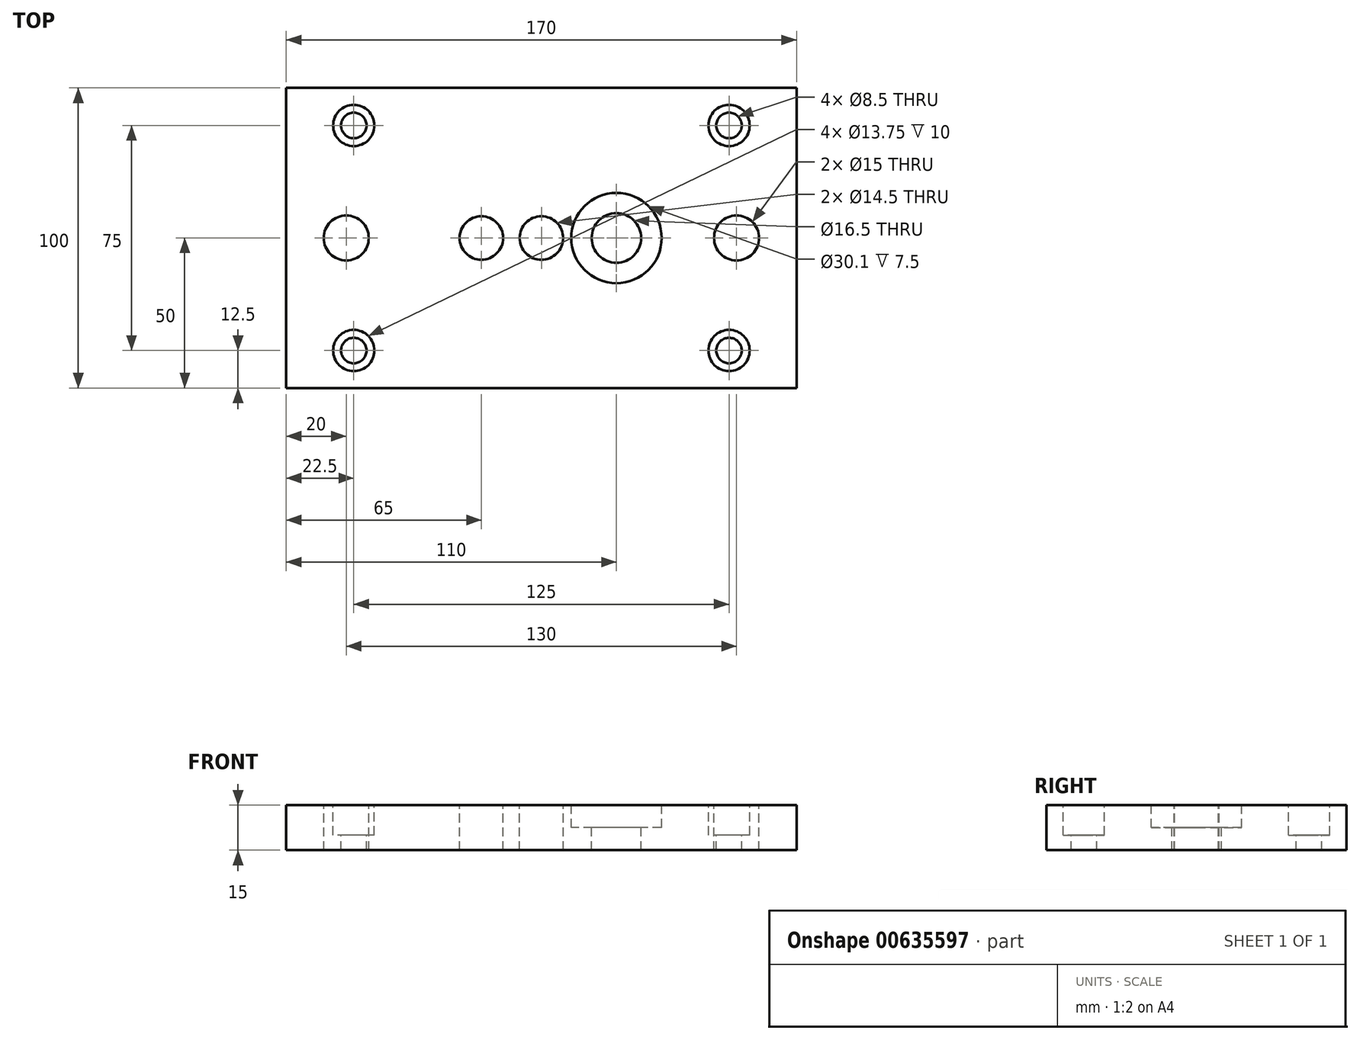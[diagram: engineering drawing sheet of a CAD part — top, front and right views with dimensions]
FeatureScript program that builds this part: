
annotation { "Feature Type Name" : "Feature", "Feature Type Description" : "" }
export const myFeature = defineFeature(function(context is Context, id is Id, definition is map)
    precondition{}
    {
        {
            var Q0;
            Q0=qCreatedBy(makeId("Top.planeOp"),FACE);
            var sketch = newSketch(context, id + "F0", { "sketchPlane" : qUnion([Q0])});
            skLineSegment(sketch, "E0.bottom", {"start": v(0, 0) * mm, "end": v(170, 0) * mm});
            skLineSegment(sketch, "E0.top", {"start": v(0, 100) * mm, "end": v(170, 100) * mm});
            skLineSegment(sketch, "E0.left", {"start": v(0, 0) * mm, "end": v(0, 100) * mm});
            skLineSegment(sketch, "E0.right", {"start": v(170, 0) * mm, "end": v(170, 100) * mm});
            skSolve(sketch);
        }
        {
            var Q0;
            Q0=makeQuery(id+"F0.imprint","IMPRINT",FACE,{"disambiguationData":[TD([[makeQuery(id+"F0.imprint","IMPRINT",EDGE,{"derivedFrom":sQuery(id+"F0.wireOp",EDGE,"E0.bottom")}),1.0]])]});
            extrude(context, id + "F1", {"entities" : qUnion([Q0]), "oppositeDirection" : true, "depth" : 15 * mm, "offsetDistance" : 25 * mm});
        }
        {
            var Q0;
            Q0=makeQuery(id+"F1.opExtrude","CAP_FACE",FACE,{"disambiguationData":[OSD([sQuery(id+"F0.wireOp",EDGE,"E0.bottom"),sQuery(id+"F0.wireOp",EDGE,"E0.top"),sQuery(id+"F0.wireOp",EDGE,"E0.left"),sQuery(id+"F0.wireOp",EDGE,"E0.right")])],"isStart":true});
            var sketch = newSketch(context, id + "F2", { "sketchPlane" : qUnion([Q0])});
            skPoint(sketch, "E1", {"position": v(22.5, 12.5) * mm});
            skPoint(sketch, "E2", {"position": v(22.5, 87.5) * mm});
            skPoint(sketch, "E3", {"position": v(147.5, 87.5) * mm});
            skPoint(sketch, "E4", {"position": v(147.5, 12.5) * mm});
            skSolve(sketch);
        }
        {
            var Q0;
            Q0=sQuery(id+"F2.wireOp",VERTEX,"E2");
            var Q1;
            Q1=sQuery(id+"F2.wireOp",VERTEX,"E1");
            var Q2;
            Q2=sQuery(id+"F2.wireOp",VERTEX,"E3");
            var Q3;
            Q3=sQuery(id+"F2.wireOp",VERTEX,"E4");
            var Q4;
            Q4=makeQuery(id+"F1.opExtrude","SWEPT_BODY",BODY,{"disambiguationData":[OSD([sQuery(id+"F0.wireOp",EDGE,"E0.bottom"),sQuery(id+"F0.wireOp",EDGE,"E0.top"),sQuery(id+"F0.wireOp",EDGE,"E0.left"),sQuery(id+"F0.wireOp",EDGE,"E0.right")])]});
            hole(context, id + "F3", {"style" : HoleStyle.C_BORE, "endStyle" : HoleEndStyle.THROUGH, "holeDiameter" : 8.5 * mm, "cBoreDiameter" : 13.75 * mm, "cBoreDepth" : 10 * mm, "majorDiameter" : 5 * mm, "isTappedThrough" : true, "tappedDepth" : 12.7 * mm, "tapClearance" : 3, "startFromSketch" : true, "locations" : qUnion([Q0, Q1, Q2, Q3]), "scope" : qUnion([Q4])});
        }
        {
            var Q0;
            Q0=makeQuery(id+"F1.opExtrude","CAP_FACE",FACE,{"disambiguationData":[OSD([sQuery(id+"F0.wireOp",EDGE,"E0.bottom"),sQuery(id+"F0.wireOp",EDGE,"E0.top"),sQuery(id+"F0.wireOp",EDGE,"E0.left"),sQuery(id+"F0.wireOp",EDGE,"E0.right")])],"isStart":true});
            var sketch = newSketch(context, id + "F4", { "sketchPlane" : qUnion([Q0])});
            skPoint(sketch, "E5", {"position": v(20, 50) * mm});
            skPoint(sketch, "E6", {"position": v(150, 50) * mm});
            skSolve(sketch);
        }
        {
            var Q0;
            Q0=sQuery(id+"F4.wireOp",VERTEX,"E5");
            var Q1;
            Q1=sQuery(id+"F4.wireOp",VERTEX,"E6");
            var Q2;
            Q2=makeQuery(id+"F1.opExtrude","SWEPT_BODY",BODY,{"disambiguationData":[OSD([sQuery(id+"F0.wireOp",EDGE,"E0.bottom"),sQuery(id+"F0.wireOp",EDGE,"E0.top"),sQuery(id+"F0.wireOp",EDGE,"E0.left"),sQuery(id+"F0.wireOp",EDGE,"E0.right")])]});
            hole(context, id + "F5", {"style" : HoleStyle.SIMPLE, "endStyle" : HoleEndStyle.THROUGH, "holeDiameter" : 15 * mm, "majorDiameter" : 5 * mm, "isTappedThrough" : true, "tappedDepth" : 12.7 * mm, "tapClearance" : 3, "startFromSketch" : true, "locations" : qUnion([Q0, Q1]), "scope" : qUnion([Q2])});
        }
        {
            var Q0;
            Q0=makeQuery(id+"F1.opExtrude","CAP_FACE",FACE,{"disambiguationData":[OSD([sQuery(id+"F0.wireOp",EDGE,"E0.bottom"),sQuery(id+"F0.wireOp",EDGE,"E0.top"),sQuery(id+"F0.wireOp",EDGE,"E0.left"),sQuery(id+"F0.wireOp",EDGE,"E0.right")])],"isStart":true});
            var sketch = newSketch(context, id + "F6", { "sketchPlane" : qUnion([Q0])});
            skPoint(sketch, "E7", {"position": v(65, 50) * mm});
            skPoint(sketch, "E8", {"position": v(85, 50) * mm});
            skSolve(sketch);
        }
        {
            var Q0;
            Q0=sQuery(id+"F6.wireOp",VERTEX,"E7");
            var Q1;
            Q1=sQuery(id+"F6.wireOp",VERTEX,"E8");
            var Q2;
            Q2=makeQuery(id+"F1.opExtrude","SWEPT_BODY",BODY,{"disambiguationData":[OSD([sQuery(id+"F0.wireOp",EDGE,"E0.bottom"),sQuery(id+"F0.wireOp",EDGE,"E0.top"),sQuery(id+"F0.wireOp",EDGE,"E0.left"),sQuery(id+"F0.wireOp",EDGE,"E0.right")])]});
            hole(context, id + "F7", {"style" : HoleStyle.SIMPLE, "endStyle" : HoleEndStyle.THROUGH, "holeDiameter" : 14.5 * mm, "majorDiameter" : 5 * mm, "isTappedThrough" : true, "tappedDepth" : 12.7 * mm, "tapClearance" : 3, "startFromSketch" : true, "locations" : qUnion([Q0, Q1]), "scope" : qUnion([Q2])});
        }
        {
            var Q0;
            Q0=makeQuery(id+"F1.opExtrude","CAP_FACE",FACE,{"disambiguationData":[OSD([sQuery(id+"F0.wireOp",EDGE,"E0.bottom"),sQuery(id+"F0.wireOp",EDGE,"E0.top"),sQuery(id+"F0.wireOp",EDGE,"E0.left"),sQuery(id+"F0.wireOp",EDGE,"E0.right")])],"isStart":true});
            var sketch = newSketch(context, id + "F8", { "sketchPlane" : qUnion([Q0])});
            skPoint(sketch, "E9", {"position": v(110, 50) * mm});
            skSolve(sketch);
        }
        {
            var Q0;
            Q0=sQuery(id+"F8.wireOp",VERTEX,"E9");
            var Q1;
            Q1=makeQuery(id+"F1.opExtrude","SWEPT_BODY",BODY,{"disambiguationData":[OSD([sQuery(id+"F0.wireOp",EDGE,"E0.bottom"),sQuery(id+"F0.wireOp",EDGE,"E0.top"),sQuery(id+"F0.wireOp",EDGE,"E0.left"),sQuery(id+"F0.wireOp",EDGE,"E0.right")])]});
            hole(context, id + "F9", {"style" : HoleStyle.C_BORE, "endStyle" : HoleEndStyle.THROUGH, "holeDiameter" : 16.5 * mm, "cBoreDiameter" : 30.1 * mm, "cBoreDepth" : 7.5 * mm, "majorDiameter" : 5 * mm, "isTappedThrough" : true, "tappedDepth" : 12.7 * mm, "tapClearance" : 3, "startFromSketch" : true, "locations" : qUnion([Q0]), "scope" : qUnion([Q1])});
        }
    });
